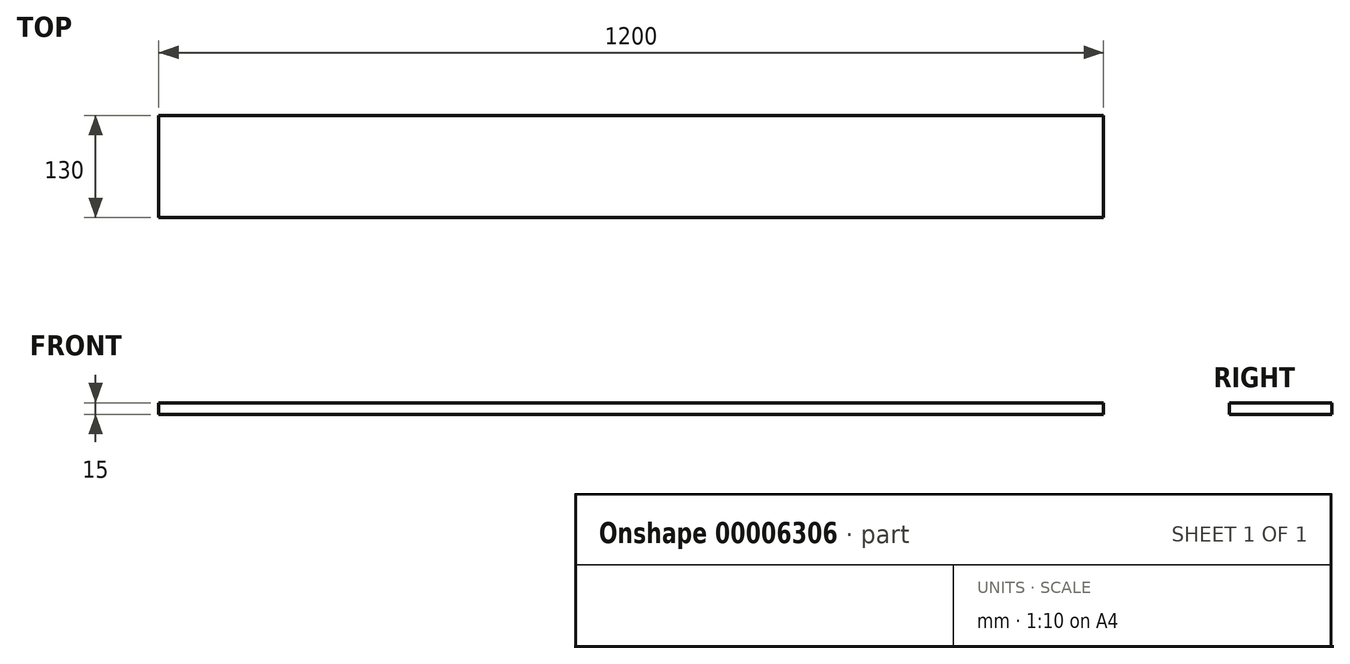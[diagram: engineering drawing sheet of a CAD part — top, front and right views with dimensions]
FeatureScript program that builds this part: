
annotation { "Feature Type Name" : "Feature", "Feature Type Description" : "" }
export const myFeature = defineFeature(function(context is Context, id is Id, definition is map)
    precondition{}
    {
        {
            var Q0;
            Q0=qCreatedBy(makeId("Top.planeOp"),FACE);
            var sketch = newSketch(context, id + "F0", { "sketchPlane" : qUnion([Q0])});
            skLineSegment(sketch, "E0.bottom", {"start": v(-167.45, 86.13) * mm, "end": v(1032.55, 86.13) * mm});
            skLineSegment(sketch, "E0.top", {"start": v(-167.45, -43.87) * mm, "end": v(1032.55, -43.87) * mm});
            skLineSegment(sketch, "E0.left", {"start": v(-167.45, 86.13) * mm, "end": v(-167.45, -43.87) * mm});
            skLineSegment(sketch, "E0.right", {"start": v(1032.55, 86.13) * mm, "end": v(1032.55, -43.87) * mm});
            skSolve(sketch);
        }
        {
            var Q0;
            Q0=makeQuery(id+"F0.imprint","IMPRINT",FACE,{"disambiguationData":[TD([[makeQuery(id+"F0.imprint","IMPRINT",EDGE,{"derivedFrom":sQuery(id+"F0.wireOp",EDGE,"E0.bottom")}),-1.0]])]});
            extrude(context, id + "F1", {"entities" : qUnion([Q0]), "depth" : 15 * mm});
        }
    });
